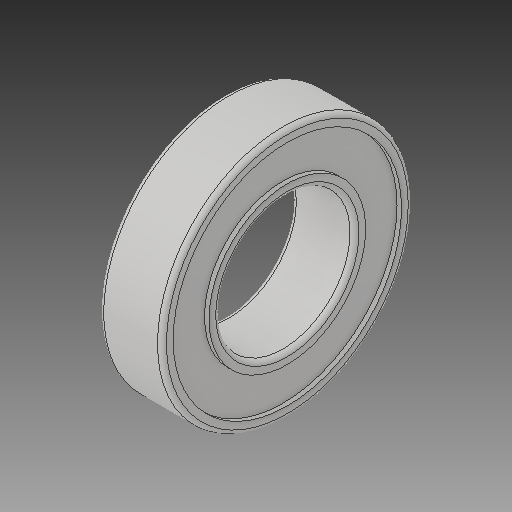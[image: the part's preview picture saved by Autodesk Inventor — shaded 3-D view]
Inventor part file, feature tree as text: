
AUTODESK INVENTOR PART (.ipt)
format: ipt  version: 2019 (Build 230136000, 136)  size: 176,640 bytes
history: native  units: in
note: dims shown in document units (in); Inventor stores cm internally (conversion verified against a paired STEP export)
features: fillet x1
ambient origin geometry x8: Origin, YZ Plane, XZ Plane, XY Plane, X Axis, Y Axis, Z Axis, Center Point
bodies: Solid1 (feature_tree)
feature tree (1):
  fillet  "Fillet1"  [1 undecoded]
note: 1 required parameter value undecoded (feature->parameter linkage not recoverable at this tier; creation-order binding heuristic only, values carry confidence <= 0.55)
